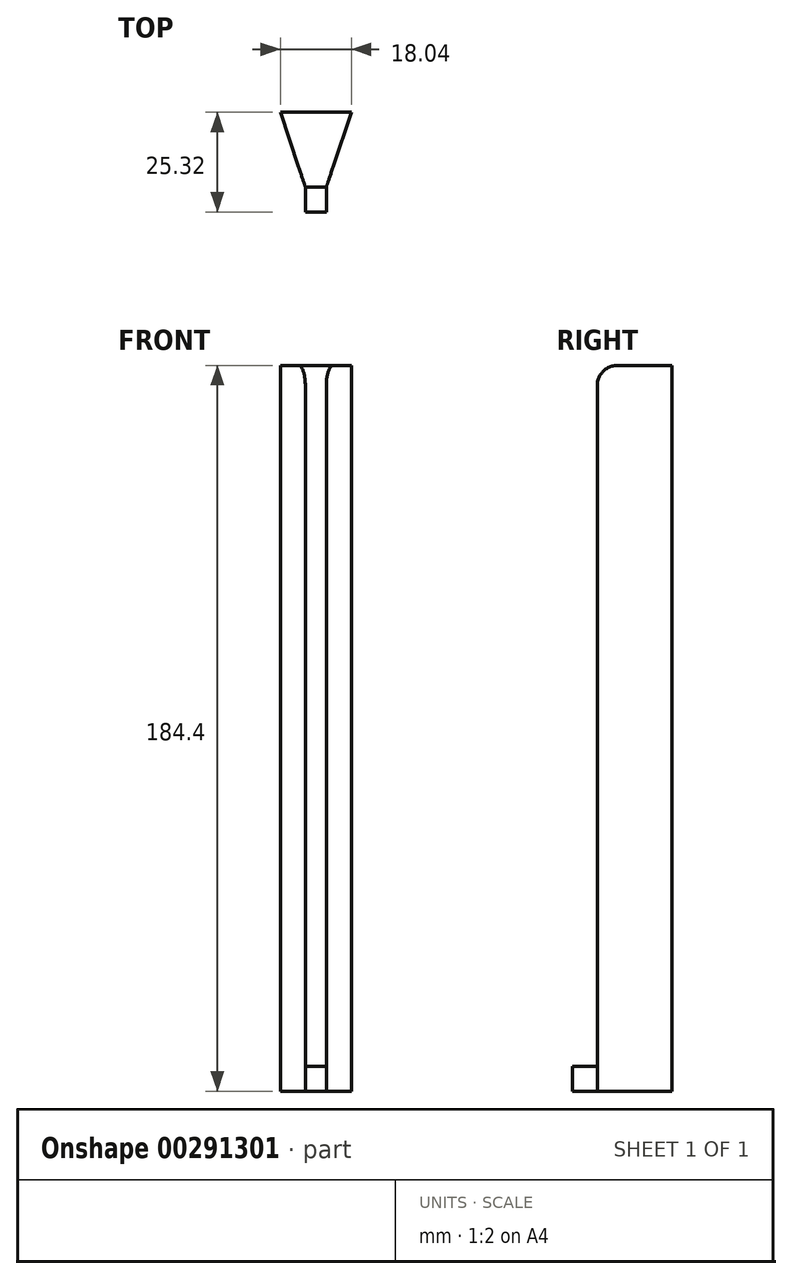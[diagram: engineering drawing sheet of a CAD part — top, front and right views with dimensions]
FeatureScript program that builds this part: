
annotation { "Feature Type Name" : "Feature", "Feature Type Description" : "" }
export const myFeature = defineFeature(function(context is Context, id is Id, definition is map)
    precondition{}
    {
        {
            var Q0;
            Q0=qCreatedBy(makeId("Top.planeOp"),FACE);
            var sketch = newSketch(context, id + "F0", { "sketchPlane" : qUnion([Q0])});
            skLineSegment(sketch, "E0", {"start": v(-9.02, -42.86) * mm, "end": v(9.02, -42.86) * mm});
            skLineSegment(sketch, "E1", {"start": v(9.02, -42.86) * mm, "end": v(2.67, -61.83) * mm});
            skLineSegment(sketch, "E2.MirrorCS", {"start": v(-9.02, -42.86) * mm, "end": v(-2.67, -61.83) * mm});
            skPoint(sketch, "E3.center", {"position": v(0, 0) * mm});
            skLineSegment(sketch, "E4.1.0", {"start": v(-2.67, -68.18) * mm, "end": v(2.67, -68.18) * mm});
            skLineSegment(sketch, "E5", {"start": v(-2.67, -61.83) * mm, "end": v(2.67, -61.83) * mm});
            skLineSegment(sketch, "E6", {"start": v(-2.67, -61.83) * mm, "end": v(-2.67, -68.18) * mm});
            skLineSegment(sketch, "E7", {"start": v(2.67, -61.83) * mm, "end": v(2.67, -68.18) * mm});
            skSolve(sketch);
        }
        {
            var Q0;
            Q0=makeQuery(id+"F0.imprint","IMPRINT",FACE,{"disambiguationData":[TD([[makeQuery(id+"F0.imprint","IMPRINT",EDGE,{"derivedFrom":sQuery(id+"F0.wireOp",EDGE,"E0")}),-1.0]])]});
            extrude(context, id + "F1", {"entities" : qUnion([Q0]), "depth" : 184.4 * mm});
        }
        {
            var Q0;
            Q0=makeQuery(id+"F0.imprint","IMPRINT",FACE,{"disambiguationData":[TD([[makeQuery(id+"F0.imprint","IMPRINT",EDGE,{"derivedFrom":sQuery(id+"F0.wireOp",EDGE,"E4.1.0")}),1.0]])]});
            extrude(context, id + "F2", {"entities" : qUnion([Q0]), "operationType" : NewBodyOperationType.ADD, "depth" : 6.35 * mm});
        }
        {
            var Q0;
            Q0=makeQuery(id+"F1.opExtrude","CAP_EDGE",EDGE,{"disambiguationData":[OSD([sQuery(id+"F0.wireOp",EDGE,"E5")])],"isStart":false});
            fillet(context, id + "F3", {"entities" : qUnion([Q0]), "radius" : 5.08 * mm, "tangentPropagation" : true, "allowEdgeOverflow" : false});
        }
    });
